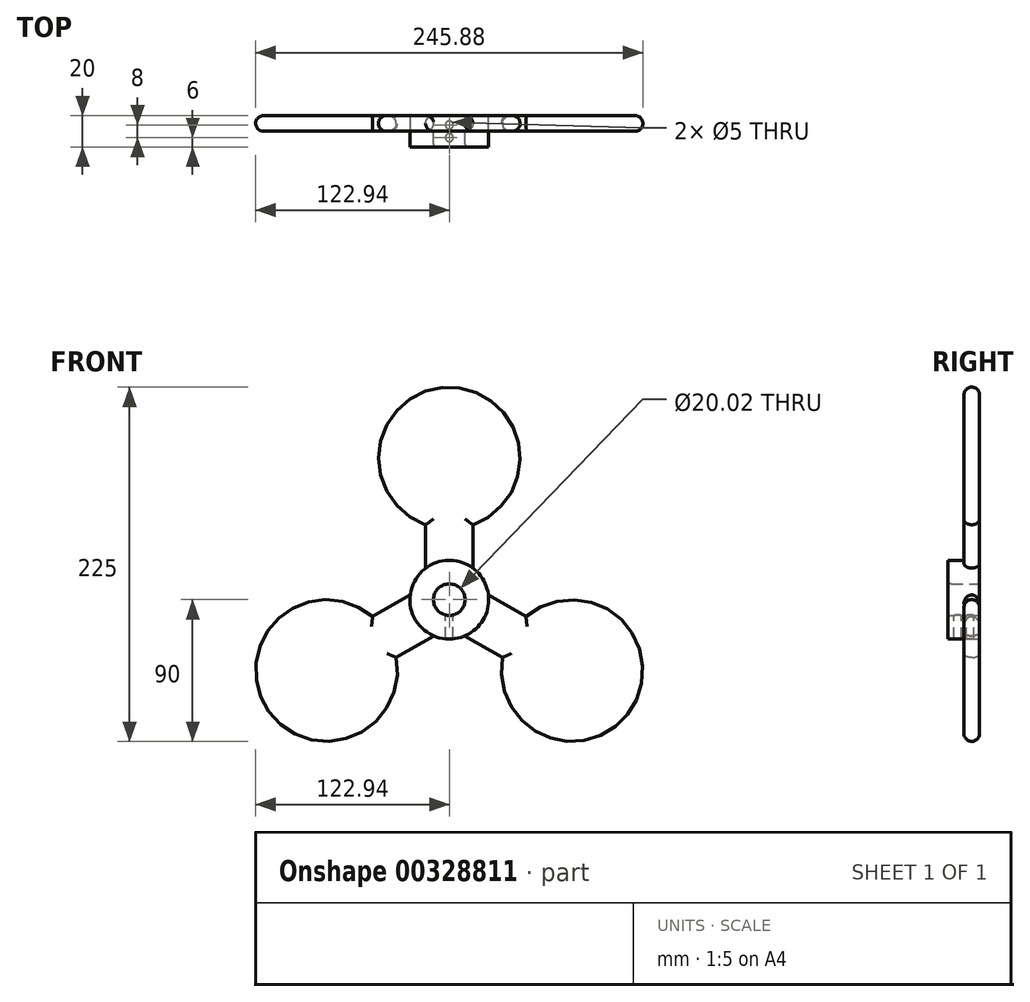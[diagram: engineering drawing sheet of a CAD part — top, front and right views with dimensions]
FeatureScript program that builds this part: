
annotation { "Feature Type Name" : "Feature", "Feature Type Description" : "" }
export const myFeature = defineFeature(function(context is Context, id is Id, definition is map)
    precondition{}
    {
        {
            var Q0;
            Q0=qCreatedBy(makeId("Front.planeOp"),FACE);
            var sketch = newSketch(context, id + "F0", { "sketchPlane" : qUnion([Q0])});
            skCircle(sketch, "E0", {"center": v(0, 0) * mm, "radius": 10 * mm});
            skCircle(sketch, "E1", {"center": v(0, 0) * mm, "radius": 90 * mm});
            skLineSegment(sketch, "E2", {"start": v(0, 90) * mm, "end": v(0, 0) * mm});
            skLineSegment(sketch, "E3", {"start": v(77.94, -45) * mm, "end": v(0, 0) * mm});
            skLineSegment(sketch, "E4", {"start": v(-77.94, -45) * mm, "end": v(0, 0) * mm});
            skCircle(sketch, "E5", {"center": v(-77.94, -45) * mm, "radius": 45 * mm});
            skCircle(sketch, "E6", {"center": v(77.94, -45) * mm, "radius": 45 * mm});
            skCircle(sketch, "E7", {"center": v(0, 90) * mm, "radius": 45 * mm});
            skCircle(sketch, "E8", {"center": v(0, 0) * mm, "radius": 25 * mm});
            skSolve(sketch);
        }
        {
            var Q0;
            {var subQ0=sQuery(id+"F0.wireOp",EDGE,"E1");var subQ1=makeQuery(id+"F0.imprint","INTERSECT",VERTEX,{"derivedFrom":[subQ0,sQuery(id+"F0.wireOp",EDGE,"E2")]});Q0=makeQuery(id+"F0.imprint","IMPRINT",FACE,{"disambiguationData":[TD([[makeQuery(id+"F0.imprint","IMPRINT",EDGE,{"disambiguationData":[TD([[subQ1,1.0]])],"derivedFrom":subQ0}),-1.0]])]});}
            var Q1;
            {var subQ0=sQuery(id+"F0.wireOp",EDGE,"E1");var subQ1=makeQuery(id+"F0.imprint","INTERSECT",VERTEX,{"derivedFrom":[subQ0,sQuery(id+"F0.wireOp",EDGE,"E4")]});Q1=makeQuery(id+"F0.imprint","IMPRINT",FACE,{"disambiguationData":[TD([[makeQuery(id+"F0.imprint","IMPRINT",EDGE,{"disambiguationData":[TD([[subQ1,1.0]])],"derivedFrom":subQ0}),-1.0]])]});}
            var Q2;
            {var subQ0=sQuery(id+"F0.wireOp",EDGE,"E1");var subQ1=makeQuery(id+"F0.imprint","INTERSECT",VERTEX,{"derivedFrom":[subQ0,sQuery(id+"F0.wireOp",EDGE,"E3")]});Q2=makeQuery(id+"F0.imprint","IMPRINT",FACE,{"disambiguationData":[TD([[makeQuery(id+"F0.imprint","IMPRINT",EDGE,{"disambiguationData":[TD([[subQ1,1.0]])],"derivedFrom":subQ0}),-1.0]])]});}
            var Q3;
            {var subQ0=sQuery(id+"F0.wireOp",EDGE,"E2");var subQ1=sQuery(id+"F0.wireOp",EDGE,"E1");var subQ2=makeQuery(id+"F0.imprint","INTERSECT",VERTEX,{"derivedFrom":[subQ1,subQ0]});Q3=makeQuery(id+"F0.imprint","IMPRINT",FACE,{"disambiguationData":[TD([[makeQuery(id+"F0.imprint","IMPRINT",EDGE,{"disambiguationData":[TD([[subQ2,-1.0]])],"derivedFrom":subQ1}),1.0]])]});}
            var Q4;
            {var subQ0=sQuery(id+"F0.wireOp",EDGE,"E4");var subQ1=sQuery(id+"F0.wireOp",EDGE,"E1");var subQ2=makeQuery(id+"F0.imprint","INTERSECT",VERTEX,{"derivedFrom":[subQ1,subQ0]});Q4=makeQuery(id+"F0.imprint","IMPRINT",FACE,{"disambiguationData":[TD([[makeQuery(id+"F0.imprint","IMPRINT",EDGE,{"disambiguationData":[TD([[subQ2,1.0]])],"derivedFrom":subQ1}),1.0]])]});}
            var Q5;
            {var subQ0=sQuery(id+"F0.wireOp",EDGE,"E4");var subQ1=sQuery(id+"F0.wireOp",EDGE,"E1");var subQ2=makeQuery(id+"F0.imprint","INTERSECT",VERTEX,{"derivedFrom":[subQ1,subQ0]});Q5=makeQuery(id+"F0.imprint","IMPRINT",FACE,{"disambiguationData":[TD([[makeQuery(id+"F0.imprint","IMPRINT",EDGE,{"disambiguationData":[TD([[subQ2,-1.0]])],"derivedFrom":subQ1}),1.0]])]});}
            var Q6;
            {var subQ0=sQuery(id+"F0.wireOp",EDGE,"E3");var subQ1=sQuery(id+"F0.wireOp",EDGE,"E1");var subQ2=makeQuery(id+"F0.imprint","INTERSECT",VERTEX,{"derivedFrom":[subQ1,subQ0]});Q6=makeQuery(id+"F0.imprint","IMPRINT",FACE,{"disambiguationData":[TD([[makeQuery(id+"F0.imprint","IMPRINT",EDGE,{"disambiguationData":[TD([[subQ2,1.0]])],"derivedFrom":subQ1}),1.0]])]});}
            var Q7;
            {var subQ0=sQuery(id+"F0.wireOp",EDGE,"E3");var subQ1=sQuery(id+"F0.wireOp",EDGE,"E1");var subQ2=makeQuery(id+"F0.imprint","INTERSECT",VERTEX,{"derivedFrom":[subQ1,subQ0]});Q7=makeQuery(id+"F0.imprint","IMPRINT",FACE,{"disambiguationData":[TD([[makeQuery(id+"F0.imprint","IMPRINT",EDGE,{"disambiguationData":[TD([[subQ2,-1.0]])],"derivedFrom":subQ1}),1.0]])]});}
            var Q8;
            {var subQ0=sQuery(id+"F0.wireOp",EDGE,"E2");var subQ1=sQuery(id+"F0.wireOp",EDGE,"E0");var subQ2=makeQuery(id+"F0.imprint","INTERSECT",VERTEX,{"derivedFrom":[subQ1,subQ0]});Q8=makeQuery(id+"F0.imprint","IMPRINT",FACE,{"disambiguationData":[TD([[makeQuery(id+"F0.imprint","IMPRINT",EDGE,{"disambiguationData":[TD([[subQ2,1.0]])],"derivedFrom":subQ1}),-1.0]])]});}
            var Q9;
            {var subQ0=sQuery(id+"F0.wireOp",EDGE,"E4");var subQ1=sQuery(id+"F0.wireOp",EDGE,"E0");var subQ2=makeQuery(id+"F0.imprint","INTERSECT",VERTEX,{"derivedFrom":[subQ1,subQ0]});Q9=makeQuery(id+"F0.imprint","IMPRINT",FACE,{"disambiguationData":[TD([[makeQuery(id+"F0.imprint","IMPRINT",EDGE,{"disambiguationData":[TD([[subQ2,-1.0]])],"derivedFrom":subQ1}),-1.0]])]});}
            var Q10;
            {var subQ0=sQuery(id+"F0.wireOp",EDGE,"E4");var subQ1=sQuery(id+"F0.wireOp",EDGE,"E0");var subQ2=makeQuery(id+"F0.imprint","INTERSECT",VERTEX,{"derivedFrom":[subQ1,subQ0]});Q10=makeQuery(id+"F0.imprint","IMPRINT",FACE,{"disambiguationData":[TD([[makeQuery(id+"F0.imprint","IMPRINT",EDGE,{"disambiguationData":[TD([[subQ2,1.0]])],"derivedFrom":subQ1}),-1.0]])]});}
            var Q11;
            {var subQ0=sQuery(id+"F0.wireOp",EDGE,"E2");var subQ1=sQuery(id+"F0.wireOp",EDGE,"E1");var subQ2=makeQuery(id+"F0.imprint","INTERSECT",VERTEX,{"derivedFrom":[subQ1,subQ0]});Q11=makeQuery(id+"F0.imprint","IMPRINT",FACE,{"disambiguationData":[TD([[makeQuery(id+"F0.imprint","IMPRINT",EDGE,{"disambiguationData":[TD([[subQ2,1.0]])],"derivedFrom":subQ1}),1.0]])]});}
            extrude(context, id + "F1", {"entities" : qUnion([Q0, Q1, Q2, Q3, Q4, Q5, Q6, Q7, Q8, Q9, Q10, Q11]), "depth" : 10 * mm});
        }
        {
            var Q0;
            Q0=qCreatedBy(makeId("Front.planeOp"),FACE);
            var sketch = newSketch(context, id + "F2", { "sketchPlane" : qUnion([Q0])});
            skLineSegment(sketch, "E9", {"start": v(0, 0) * mm, "end": v(0, 198.43) * mm});
            skLineSegment(sketch, "E10", {"start": v(0, 0) * mm, "end": v(173.29, -100.05) * mm});
            skLineSegment(sketch, "E11", {"start": v(-15, 55.5) * mm, "end": v(-15, 14.08) * mm});
            skLineSegment(sketch, "E12", {"start": v(15, 55.5) * mm, "end": v(15, 14.08) * mm});
            skLineSegment(sketch, "E13", {"start": v(-15, 55.5) * mm, "end": v(15, 55.5) * mm});
            skLineSegment(sketch, "E14", {"start": v(-15, 14.08) * mm, "end": v(15, 14.08) * mm});
            skLineSegment(sketch, "E15", {"start": v(19.95, 5.8) * mm, "end": v(4.95, -20.18) * mm});
            skLineSegment(sketch, "E16", {"start": v(63.9, -19.58) * mm, "end": v(48.9, -45.56) * mm});
            skLineSegment(sketch, "E17", {"start": v(19.95, 5.8) * mm, "end": v(63.9, -19.58) * mm});
            skLineSegment(sketch, "E18", {"start": v(4.95, -20.18) * mm, "end": v(48.9, -45.56) * mm});
            skLineSegment(sketch, "E19", {"start": v(0, 0) * mm, "end": v(-116, -66.97) * mm});
            skLineSegment(sketch, "E20", {"start": v(-19.57, 6.02) * mm, "end": v(-4.57, -19.96) * mm});
            skLineSegment(sketch, "E21", {"start": v(-64.44, -19.88) * mm, "end": v(-49.44, -45.86) * mm});
            skLineSegment(sketch, "E22", {"start": v(-19.57, 6.02) * mm, "end": v(-64.44, -19.88) * mm});
            skLineSegment(sketch, "E23", {"start": v(-49.44, -45.86) * mm, "end": v(-4.57, -19.96) * mm});
            skSolve(sketch);
        }
        {
            var Q0;
            {var subQ5=sQuery(id+"F2.wireOp",EDGE,"E11");Q0=makeQuery(id+"F2.imprint","IMPRINT",FACE,{"disambiguationData":[TD([[makeQuery(id+"F2.imprint","IMPRINT",EDGE,{"derivedFrom":subQ5}),1.0]])]});}
            var Q1;
            {var subQ5=sQuery(id+"F2.wireOp",EDGE,"E12");Q1=makeQuery(id+"F2.imprint","IMPRINT",FACE,{"disambiguationData":[TD([[makeQuery(id+"F2.imprint","IMPRINT",EDGE,{"derivedFrom":subQ5}),-1.0]])]});}
            var Q2;
            {var subQ5=sQuery(id+"F2.wireOp",EDGE,"E18");Q2=makeQuery(id+"F2.imprint","IMPRINT",FACE,{"disambiguationData":[TD([[makeQuery(id+"F2.imprint","IMPRINT",EDGE,{"derivedFrom":subQ5}),1.0]])]});}
            var Q3;
            {var subQ5=sQuery(id+"F2.wireOp",EDGE,"E17");Q3=makeQuery(id+"F2.imprint","IMPRINT",FACE,{"disambiguationData":[TD([[makeQuery(id+"F2.imprint","IMPRINT",EDGE,{"derivedFrom":subQ5}),-1.0]])]});}
            var Q4;
            {var subQ5=sQuery(id+"F2.wireOp",EDGE,"E23");Q4=makeQuery(id+"F2.imprint","IMPRINT",FACE,{"disambiguationData":[TD([[makeQuery(id+"F2.imprint","IMPRINT",EDGE,{"derivedFrom":subQ5}),1.0]])]});}
            var Q5;
            {var subQ5=sQuery(id+"F2.wireOp",EDGE,"E22");Q5=makeQuery(id+"F2.imprint","IMPRINT",FACE,{"disambiguationData":[TD([[makeQuery(id+"F2.imprint","IMPRINT",EDGE,{"derivedFrom":subQ5}),1.0]])]});}
            extrude(context, id + "F3", {"entities" : qUnion([Q0, Q1, Q2, Q3, Q4, Q5]), "operationType" : NewBodyOperationType.ADD, "depth" : 10 * mm});
        }
        {
            var Q0;
            Q0=makeQuery(id+"F1.opExtrude","CAP_EDGE",EDGE,{"disambiguationData":[OSD([sQuery(id+"F0.wireOp",EDGE,"E7")])],"isStart":false});
            var Q1;
            Q1=makeQuery(id+"F1.opExtrude","CAP_EDGE",EDGE,{"disambiguationData":[OSD([sQuery(id+"F0.wireOp",EDGE,"E7")])],"isStart":true});
            var Q2;
            Q2=makeQuery(id+"F1.opExtrude","CAP_EDGE",EDGE,{"disambiguationData":[OSD([sQuery(id+"F0.wireOp",EDGE,"E6")])],"isStart":false});
            var Q3;
            Q3=makeQuery(id+"F1.opExtrude","CAP_EDGE",EDGE,{"disambiguationData":[OSD([sQuery(id+"F0.wireOp",EDGE,"E6")])],"isStart":true});
            var Q4;
            Q4=makeQuery(id+"F1.opExtrude","CAP_EDGE",EDGE,{"disambiguationData":[OSD([sQuery(id+"F0.wireOp",EDGE,"E5")])],"isStart":false});
            var Q5;
            Q5=makeQuery(id+"F1.opExtrude","CAP_EDGE",EDGE,{"disambiguationData":[OSD([sQuery(id+"F0.wireOp",EDGE,"E5")])],"isStart":true});
            fillet(context, id + "F4", {"entities" : qUnion([Q0, Q1, Q2, Q3, Q4, Q5]), "radius" : 5 * mm, "tangentPropagation" : true, "allowEdgeOverflow" : false});
        }
        {
            var Q0;
            Q0=makeQuery(id+"F3.boolean.opBoolean","MERGE",FACE,{"derivedFrom":[makeQuery(id+"F1.opExtrude","CAP_FACE",FACE,{"disambiguationData":[OSD([sQuery(id+"F0.wireOp",EDGE,"E0"),sQuery(id+"F0.wireOp",EDGE,"E8")])],"isStart":false}),makeQuery(id+"F1.opExtrude","CAP_FACE",FACE,{"disambiguationData":[OSD([sQuery(id+"F0.wireOp",EDGE,"E5")])],"isStart":false}),makeQuery(id+"F1.opExtrude","CAP_FACE",FACE,{"disambiguationData":[OSD([sQuery(id+"F0.wireOp",EDGE,"E6")])],"isStart":false}),makeQuery(id+"F1.opExtrude","CAP_FACE",FACE,{"disambiguationData":[OSD([sQuery(id+"F0.wireOp",EDGE,"E7")])],"isStart":false}),makeQuery(id+"F3.opExtrude","CAP_FACE",FACE,{"disambiguationData":[OSD([sQuery(id+"F2.wireOp",EDGE,"E11"),sQuery(id+"F2.wireOp",EDGE,"E12"),sQuery(id+"F2.wireOp",EDGE,"E13"),sQuery(id+"F2.wireOp",EDGE,"E14")])],"isStart":false}),makeQuery(id+"F3.opExtrude","CAP_FACE",FACE,{"disambiguationData":[OSD([sQuery(id+"F2.wireOp",EDGE,"E15"),sQuery(id+"F2.wireOp",EDGE,"E16"),sQuery(id+"F2.wireOp",EDGE,"E17"),sQuery(id+"F2.wireOp",EDGE,"E18")])],"isStart":false}),makeQuery(id+"F3.opExtrude","CAP_FACE",FACE,{"disambiguationData":[OSD([sQuery(id+"F2.wireOp",EDGE,"E20"),sQuery(id+"F2.wireOp",EDGE,"E21"),sQuery(id+"F2.wireOp",EDGE,"E22"),sQuery(id+"F2.wireOp",EDGE,"E23")])],"isStart":false})]});
            var sketch = newSketch(context, id + "F5", { "sketchPlane" : qUnion([Q0])});
            skCircle(sketch, "E24", {"center": v(0, 0) * mm, "radius": 10 * mm});
            skCircle(sketch, "E25", {"center": v(0, 0) * mm, "radius": 25 * mm});
            skSolve(sketch);
        }
        {
            var Q0;
            Q0 = qSketchRegion(id + "F5", true);
            extrude(context, id + "F6", {"entities" : qUnion([Q0]), "operationType" : NewBodyOperationType.ADD, "depth" : 10 * mm});
        }
        {
            var Q0;
            Q0=makeQuery(id+"F3.opExtrude","CAP_EDGE",EDGE,{"disambiguationData":[OSD([sQuery(id+"F2.wireOp",EDGE,"E12")])],"isStart":false});
            var Q1;
            Q1=makeQuery(id+"F3.opExtrude","CAP_EDGE",EDGE,{"disambiguationData":[OSD([sQuery(id+"F2.wireOp",EDGE,"E17")])],"isStart":false});
            var Q2;
            Q2=makeQuery(id+"F3.opExtrude","CAP_EDGE",EDGE,{"disambiguationData":[OSD([sQuery(id+"F2.wireOp",EDGE,"E18")])],"isStart":false});
            var Q3;
            Q3=makeQuery(id+"F3.opExtrude","CAP_EDGE",EDGE,{"disambiguationData":[OSD([sQuery(id+"F2.wireOp",EDGE,"E23")])],"isStart":false});
            var Q4;
            Q4=makeQuery(id+"F3.opExtrude","CAP_EDGE",EDGE,{"disambiguationData":[OSD([sQuery(id+"F2.wireOp",EDGE,"E22")])],"isStart":false});
            var Q5;
            Q5=makeQuery(id+"F3.opExtrude","CAP_EDGE",EDGE,{"disambiguationData":[OSD([sQuery(id+"F2.wireOp",EDGE,"E11")])],"isStart":false});
            var Q6;
            Q6=makeQuery(id+"F3.opExtrude","CAP_EDGE",EDGE,{"disambiguationData":[OSD([sQuery(id+"F2.wireOp",EDGE,"E11")])],"isStart":true});
            var Q7;
            Q7=makeQuery(id+"F3.opExtrude","CAP_EDGE",EDGE,{"disambiguationData":[OSD([sQuery(id+"F2.wireOp",EDGE,"E22")])],"isStart":true});
            var Q8;
            Q8=makeQuery(id+"F3.opExtrude","CAP_EDGE",EDGE,{"disambiguationData":[OSD([sQuery(id+"F2.wireOp",EDGE,"E23")])],"isStart":true});
            var Q9;
            Q9=makeQuery(id+"F3.opExtrude","CAP_EDGE",EDGE,{"disambiguationData":[OSD([sQuery(id+"F2.wireOp",EDGE,"E18")])],"isStart":true});
            var Q10;
            Q10=makeQuery(id+"F3.opExtrude","CAP_EDGE",EDGE,{"disambiguationData":[OSD([sQuery(id+"F2.wireOp",EDGE,"E17")])],"isStart":true});
            var Q11;
            Q11=makeQuery(id+"F3.opExtrude","CAP_EDGE",EDGE,{"disambiguationData":[OSD([sQuery(id+"F2.wireOp",EDGE,"E12")])],"isStart":true});
            fillet(context, id + "F7", {"entities" : qUnion([Q0, Q1, Q2, Q3, Q4, Q5, Q6, Q7, Q8, Q9, Q10, Q11]), "radius" : 5 * mm, "tangentPropagation" : true, "allowEdgeOverflow" : false});
        }
        {
            var Q0;
            Q0=makeQuery(id+"F6.opExtrude","CAP_EDGE",EDGE,{"disambiguationData":[OSD([sQuery(id+"F5.wireOp",EDGE,"E24")])],"isStart":false});
            var Q1;
            Q1=makeQuery(id+"F1.opExtrude","CAP_EDGE",EDGE,{"disambiguationData":[OSD([sQuery(id+"F0.wireOp",EDGE,"E0")])],"isStart":true});
            fillet(context, id + "F8", {"entities" : qUnion([Q0, Q1]), "radius" : 2 * mm, "tangentPropagation" : true, "allowEdgeOverflow" : false});
        }
        {
            var Q0;
            Q0=qCreatedBy(makeId("Top.planeOp"),FACE);
            var sketch = newSketch(context, id + "F9", { "sketchPlane" : qUnion([Q0])});
            skCircle(sketch, "E26", {"center": v(0, -14) * mm, "radius": 2.5 * mm});
            skCircle(sketch, "E27", {"center": v(0, -6) * mm, "radius": 2.5 * mm});
            skSolve(sketch);
        }
        {
            var Q0;
            Q0=makeQuery(id+"F9.imprint","IMPRINT",FACE,{"disambiguationData":[TD([[makeQuery(id+"F9.imprint","IMPRINT",EDGE,{"derivedFrom":sQuery(id+"F9.wireOp",EDGE,"E26")}),1.0]])]});
            var Q1;
            Q1=makeQuery(id+"F9.imprint","IMPRINT",FACE,{"disambiguationData":[TD([[makeQuery(id+"F9.imprint","IMPRINT",EDGE,{"derivedFrom":sQuery(id+"F9.wireOp",EDGE,"E27")}),1.0]])]});
            extrude(context, id + "F10", {"entities" : qUnion([Q0, Q1]), "operationType" : NewBodyOperationType.REMOVE, "oppositeDirection" : true, "depth" : 25 * mm});
        }
    });
